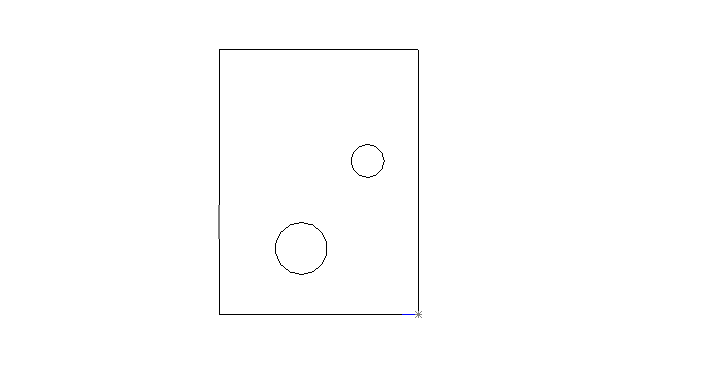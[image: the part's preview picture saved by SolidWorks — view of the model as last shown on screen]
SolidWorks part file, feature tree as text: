
SOLIDWORKS PART (.sldprt)
format: sldprt  version: not decoded by parser v0  size: 188,928 bytes
history: native  units: mm
features: sketch x4, cut_extrude x2, extrude x1 (+11 scaffold rows collapsed)
feature tree (18):
  scaffold x11  (default folders/planes/origin — collapsed)
  sketch  "Sketch1"  dims[D1=38.1mm D2=38.1mm D3=3.175mm]
  extrude  "Extrude1"  Depth=50.8mm
  sketch  "Sketch2"  dims[c1.D1=9.9822mm c1.D4=6.35mm c1.D2=12.7mm c1.D3=15.748mm c1.D5=12.7mm c1.D6=21.336mm c2.D5=28.448mm c2.D7=12.7mm c2.D8=16.764mm]
  cut_extrude  "Cut-Extrude1"  [1 undecoded]
  sketch  "Sketch3"  dims[D1=6.35mm D2=23.368mm D3=17.78mm]
  cut_extrude  "Cut-Extrude2"  [1 undecoded]
  sketch  "Sketch4"  dims[D1=~0.134113mm]
decode coverage: 5 of 7 modeling features carry decoded parameters
note: ~ marks probable driven/reference dimensions
note: 2 parameter values undecoded
note: suppression state not decoded; provenance and decode notes live in map.json
